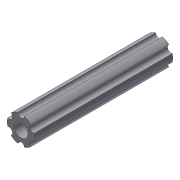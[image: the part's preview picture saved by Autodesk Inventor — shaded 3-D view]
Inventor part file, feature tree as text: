
AUTODESK INVENTOR PART (.ipt)
format: ipt  version: 2012 (Build 160160000, 160)  size: 95,232 bytes
history: native  units: in
note: dims shown in document units (in); Inventor stores cm internally (conversion verified against a paired STEP export)
features: extrude x2, sketch x2, pattern_circular x1
ambient origin geometry x8: Origin, YZ Plane, XZ Plane, XY Plane, X Axis, Y Axis, Z Axis, Center Point
bodies: Solid1 (feature_tree)
feature tree (5):
  extrude  "Extrusion1"  Depth=0.25in
  extrude  "Extrusion2"  Depth=0.0625in
  pattern_circular  "Circular Pattern1"  [2 undecoded]
  sketch  "Sketch1"  dims[d0=0.5in d1=0.25in]
  sketch  "Sketch2"  dims[d2=2.5in d3=0.0in d4=0.0625in d5=1.0in d6=0.0in d7=2.3622in d8=360.0deg]
note: 2 required parameter values undecoded (feature->parameter linkage not recoverable at this tier; creation-order binding heuristic only, values carry confidence <= 0.55)
